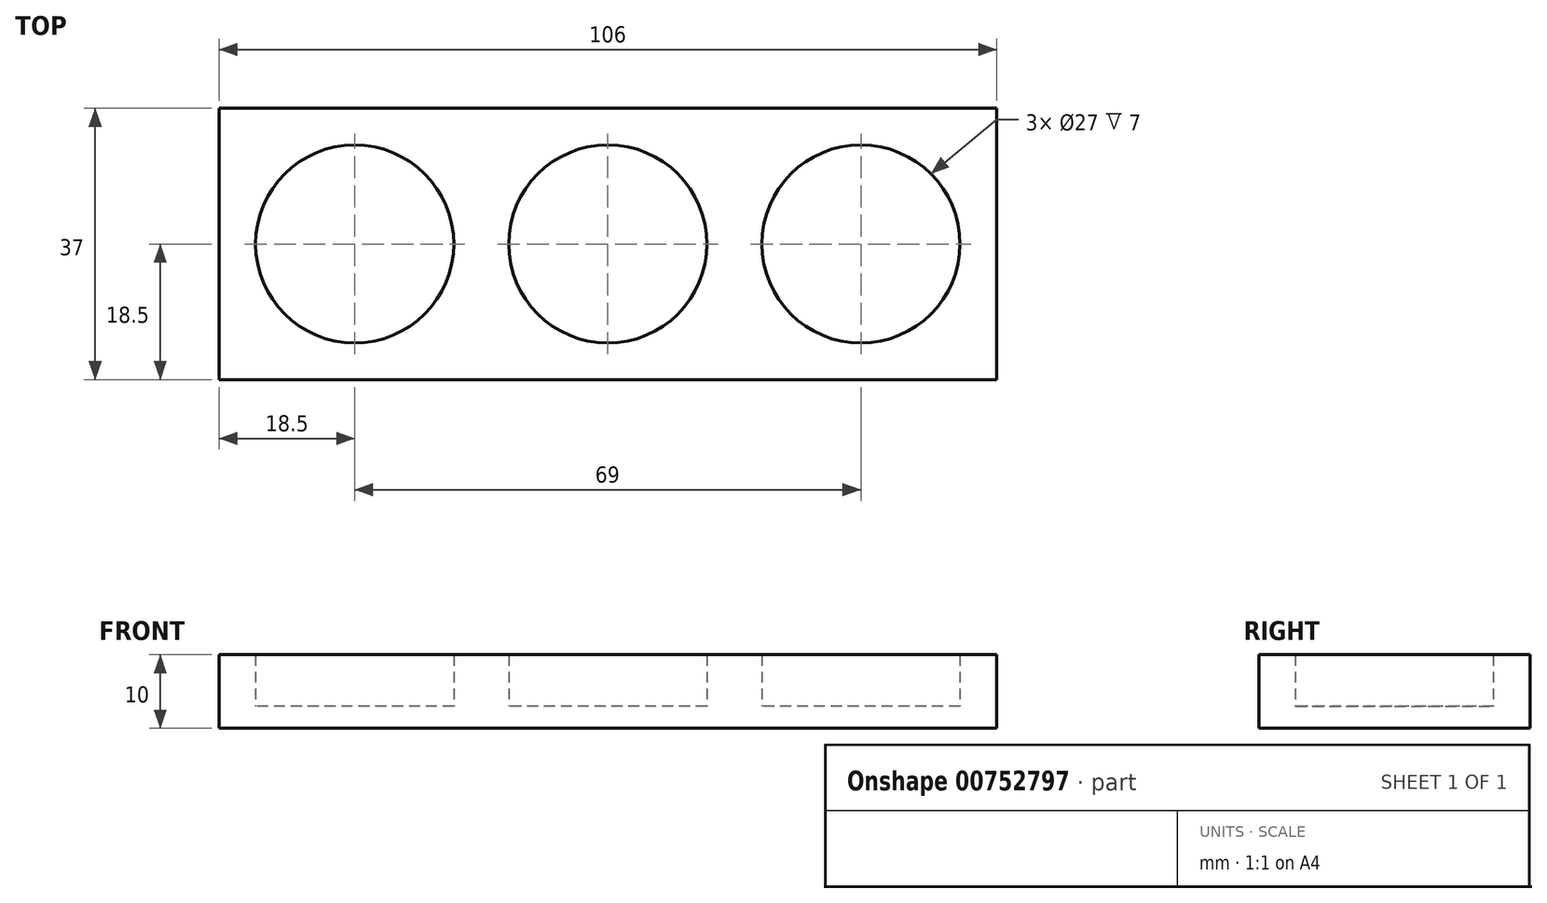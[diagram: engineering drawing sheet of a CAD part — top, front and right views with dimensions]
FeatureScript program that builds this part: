
annotation { "Feature Type Name" : "Feature", "Feature Type Description" : "" }
export const myFeature = defineFeature(function(context is Context, id is Id, definition is map)
    precondition{}
    {
        {
            var Q0;
            Q0=qCreatedBy(makeId("Top.planeOp"),FACE);
            var sketch = newSketch(context, id + "F0", { "sketchPlane" : qUnion([Q0])});
            skCircle(sketch, "E0", {"center": v(-34.5, 0) * mm, "radius": 13.5 * mm});
            skCircle(sketch, "E1", {"center": v(34.5, 0) * mm, "radius": 13.5 * mm});
            skLineSegment(sketch, "E2.bottom", {"start": v(-53, 18.5) * mm, "end": v(53, 18.5) * mm});
            skLineSegment(sketch, "E2.top", {"start": v(-53, -18.5) * mm, "end": v(53, -18.5) * mm});
            skLineSegment(sketch, "E2.left", {"start": v(-53, 18.5) * mm, "end": v(-53, -18.5) * mm});
            skLineSegment(sketch, "E2.right", {"start": v(53, 18.5) * mm, "end": v(53, -18.5) * mm});
            skCircle(sketch, "E3", {"center": v(0, 0) * mm, "radius": 13.5 * mm});
            skSolve(sketch);
        }
        {
            var Q0;
            Q0 = qSketchRegion(id + "F0", true);
            extrude(context, id + "F1", {"entities" : qUnion([Q0]), "depth" : 10 * mm, "offsetDistance" : 25 * mm});
        }
        {
            var Q0;
            Q0=makeQuery(id+"F0.imprint","IMPRINT",FACE,{"disambiguationData":[TD([[makeQuery(id+"F0.imprint","IMPRINT",EDGE,{"derivedFrom":sQuery(id+"F0.wireOp",EDGE,"E3")}),1.0]])]});
            var Q1;
            Q1=makeQuery(id+"F0.imprint","IMPRINT",FACE,{"disambiguationData":[TD([[makeQuery(id+"F0.imprint","IMPRINT",EDGE,{"derivedFrom":sQuery(id+"F0.wireOp",EDGE,"E0")}),1.0]])]});
            var Q2;
            Q2=makeQuery(id+"F0.imprint","IMPRINT",FACE,{"disambiguationData":[TD([[makeQuery(id+"F0.imprint","IMPRINT",EDGE,{"derivedFrom":sQuery(id+"F0.wireOp",EDGE,"E1")}),1.0]])]});
            extrude(context, id + "F2", {"entities" : qUnion([Q0, Q1, Q2]), "operationType" : NewBodyOperationType.ADD, "depth" : 3 * mm, "offsetDistance" : 25 * mm});
        }
    });
